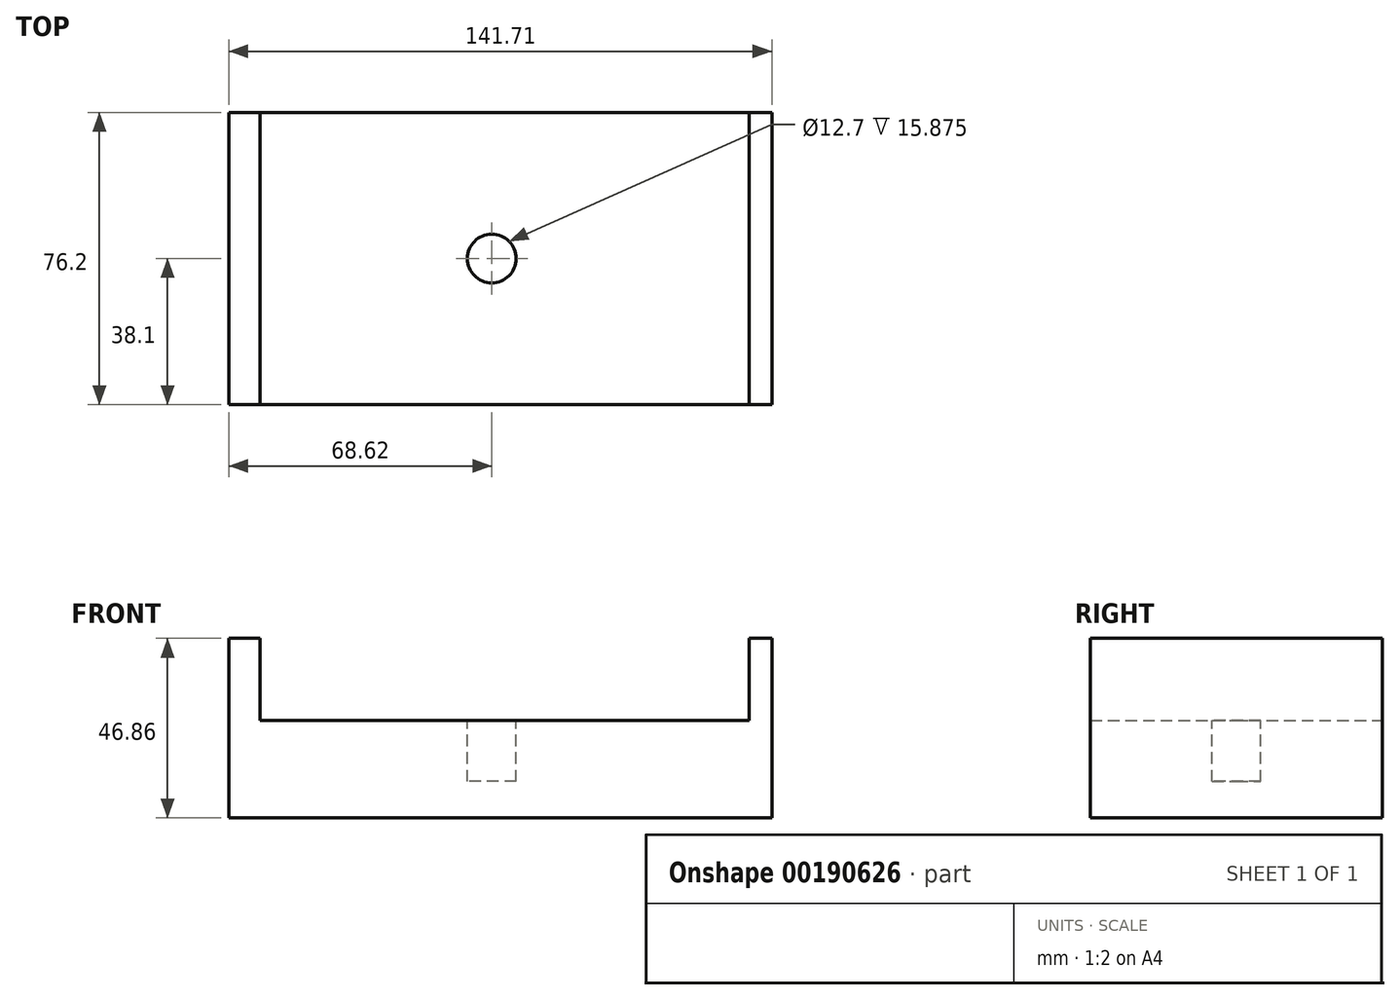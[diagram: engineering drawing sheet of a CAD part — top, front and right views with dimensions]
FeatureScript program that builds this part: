
annotation { "Feature Type Name" : "Feature", "Feature Type Description" : "" }
export const myFeature = defineFeature(function(context is Context, id is Id, definition is map)
    precondition{}
    {
        {
            var Q0;
            Q0=qCreatedBy(makeId("Front.planeOp"),FACE);
            var sketch = newSketch(context, id + "F0", { "sketchPlane" : qUnion([Q0])});
            skLineSegment(sketch, "E0", {"start": v(-68.62, 31.1) * mm, "end": v(-68.62, -15.76) * mm});
            skLineSegment(sketch, "E1", {"start": v(-68.62, -15.76) * mm, "end": v(73.1, -15.76) * mm});
            skLineSegment(sketch, "E2", {"start": v(73.1, -15.76) * mm, "end": v(73.1, 31.1) * mm});
            skLineSegment(sketch, "E3", {"start": v(73.1, 31.1) * mm, "end": v(67.16, 31.1) * mm});
            skLineSegment(sketch, "E4", {"start": v(67.16, 31.1) * mm, "end": v(67.16, 9.64) * mm});
            skLineSegment(sketch, "E5", {"start": v(67.16, 9.64) * mm, "end": v(6.35, 9.64) * mm});
            skLineSegment(sketch, "E6", {"start": v(-60.44, 9.64) * mm, "end": v(-60.44, 31.1) * mm});
            skLineSegment(sketch, "E7", {"start": v(-60.44, 31.1) * mm, "end": v(-68.62, 31.1) * mm});
            skLineSegment(sketch, "E8", {"start": v(-6.35, 9.64) * mm, "end": v(-6.35, -6.24) * mm});
            skLineSegment(sketch, "E9", {"start": v(-6.35, -6.24) * mm, "end": v(6.35, -6.24) * mm});
            skLineSegment(sketch, "E10", {"start": v(6.35, -6.24) * mm, "end": v(6.35, 9.64) * mm});
            skLineSegment(sketch, "E11.trimOffspring", {"start": v(-6.35, 9.64) * mm, "end": v(-60.44, 9.64) * mm});
            skSolve(sketch);
        }
        {
            var Q0;
            Q0 = qSketchRegion(id + "F0", true);
            extrude(context, id + "F1", {"entities" : qUnion([Q0]), "depth" : 76.2 * mm});
        }
        {
            var Q0;
            Q0=makeQuery(id+"F1.opExtrude","SWEPT_FACE",FACE,{"disambiguationData":[OSD([sQuery(id+"F0.wireOp",EDGE,"E9")])]});
            extrude(context, id + "F2", {"entities" : qUnion([Q0]), "operationType" : NewBodyOperationType.ADD, "depth" : 15.88 * mm});
        }
        {
            var Q0;
            Q0=makeQuery(id+"F2.boolean.opBoolean","MERGE",FACE,{"derivedFrom":[makeQuery(id+"F1.opExtrude","SWEPT_FACE",FACE,{"disambiguationData":[OSD([sQuery(id+"F0.wireOp",EDGE,"E5")])]}),makeQuery(id+"F1.opExtrude","SWEPT_FACE",FACE,{"disambiguationData":[OSD([sQuery(id+"F0.wireOp",EDGE,"E11.trimOffspring")])]}),makeQuery(id+"F2.opExtrude","CAP_FACE",FACE,{"disambiguationData":[OSD([sQuery(id+"F0.wireOp",EDGE,"E9")])],"isStart":false})]});
            var sketch = newSketch(context, id + "F3", { "sketchPlane" : qUnion([Q0])});
            skCircle(sketch, "E12", {"center": v(0, -38.1) * mm, "radius": 6.35 * mm});
            skSolve(sketch);
        }
        {
            var Q0;
            Q0 = qSketchRegion(id + "F3", true);
            extrude(context, id + "F4", {"entities" : qUnion([Q0]), "operationType" : NewBodyOperationType.REMOVE, "oppositeDirection" : true, "depth" : 15.88 * mm});
        }
    });
